# Revit family: Trapezblechhänger MU-B
name_source: partatom
category: Allgemeines Modell
revit_build: Autodesk Revit 2017 (Build: 20190507_1515(x64)
units: mm (PartAtom-declared; Revit-internal decimal feet)

## family parameters
Arbeitsebenenbasiert = Ja
Beim Laden mit Abzugskörper schneiden = Nein
Bemaßung runder Anschluss = Durchmesser verwenden
Gemeinsam genutzt = Nein
Immer vertikal = Nein
Kann Basisbauteil für Bewehrung sein = Nein
Raumberechnungspunkt = Nein
Teiletyp = Normal

## types (2) — shared parameters
Ausführung = Höhenregulierstück
Befestigungsloch = 9.5 mm
Breite Aufnahme (innen) = 22,5 mm
Breite Material = 25 mm
Fabrikat = MEFA
Firma = MEFA Befestigungs- und Montagesysteme GmbH
Gewicht = 0.12 kg
Gewicht pro Bauteil = 0.12 kg
Höhe = 92.5 mm
Kurztext1 = Trapezblechhänger MU-B
Material = Stahl
Materialname = S235/DD11
Mengeneinheit = St
Oberflaeche = galvanisch verzinkt
Stärke Material = 3 mm  [stored 0.00984252 ft]
Vorgabe-Ansicht = 1219 mm
max. zul. Last = 2.00 kN
vpe = 100 St

## per-type parameters (varying)
| type | Anschlussgewinde | Artikelnummer | Bundmutter | EAN | Kurztext2 |
| Trapezblechhänger MU-B M 8 | M8 | 0783803 | Bundmutter : Bundmutter M 8 (0009686) | 4250928418814 | Höhenregulierstück M8 |
| Trapezblechhänger MU-B M10 | M10 | 0783838 | Bundmutter : Bundmutter M10 (0009688) | 4250928418821 | Höhenregulierstück M10 |

note: [stored X ft] marks values corroborated as IEEE doubles in the binary element streams (Revit-internal decimal feet)
